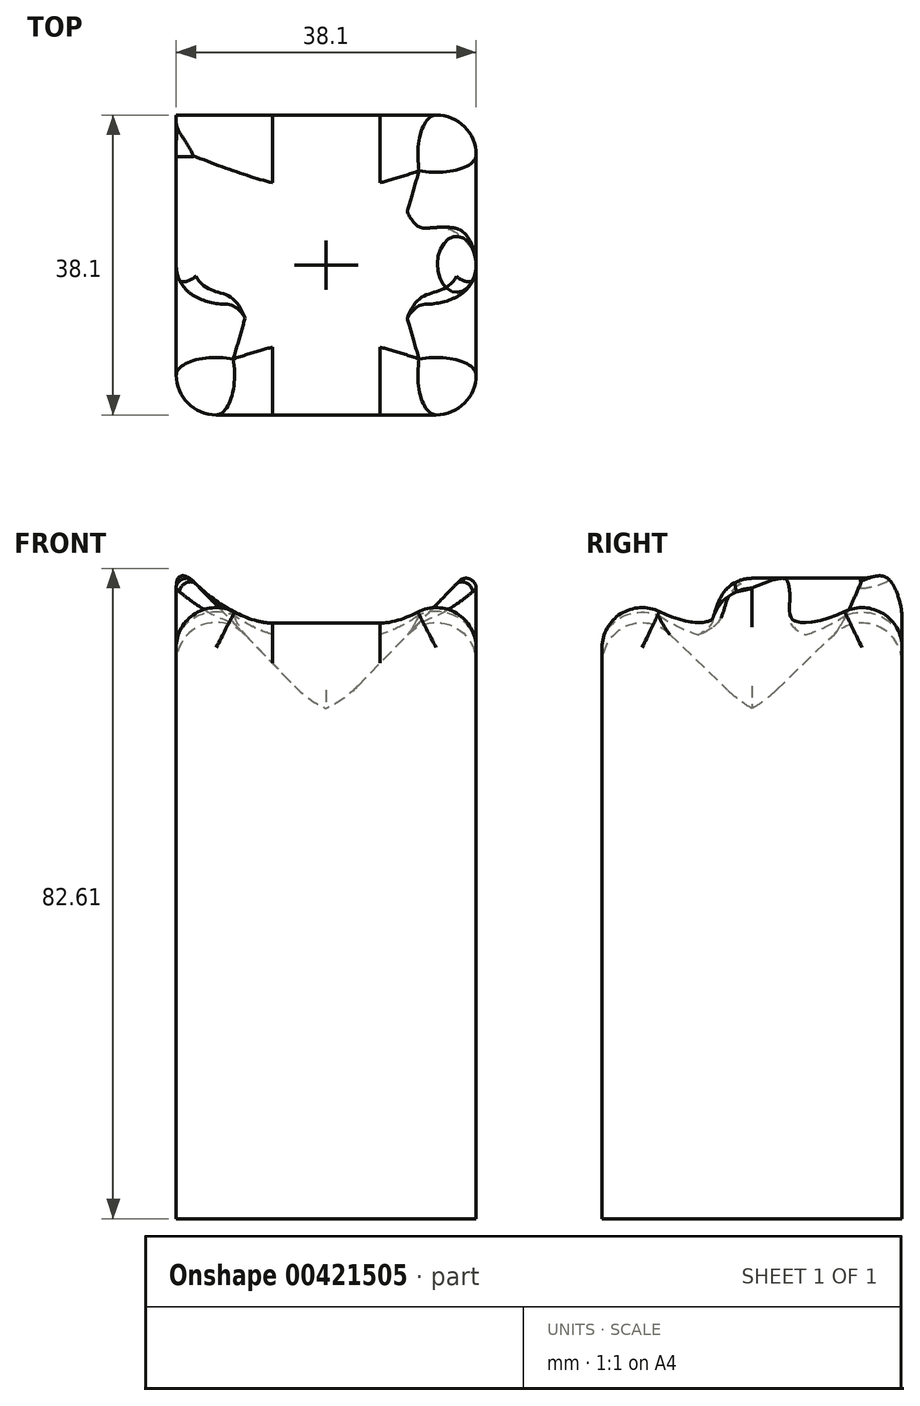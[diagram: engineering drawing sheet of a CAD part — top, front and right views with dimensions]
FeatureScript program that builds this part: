
annotation { "Feature Type Name" : "Feature", "Feature Type Description" : "" }
export const myFeature = defineFeature(function(context is Context, id is Id, definition is map)
    precondition{}
    {
        {
            var Q0;
            Q0=qCreatedBy(makeId("Top.planeOp"),FACE);
            var sketch = newSketch(context, id + "F0", { "sketchPlane" : qUnion([Q0])});
            skLineSegment(sketch, "E0.bottom", {"start": v(19.05, -19.05) * mm, "end": v(-19.05, -19.05) * mm});
            skLineSegment(sketch, "E0.top", {"start": v(19.05, 19.05) * mm, "end": v(-19.05, 19.05) * mm});
            skLineSegment(sketch, "E0.left", {"start": v(19.05, -19.05) * mm, "end": v(19.05, 19.05) * mm});
            skLineSegment(sketch, "E0.right", {"start": v(-19.05, -19.05) * mm, "end": v(-19.05, 19.05) * mm});
            skPoint(sketch, "E0.middle", {"position": v(0, 0) * mm});
            skSolve(sketch);
        }
        {
            var Q0;
            Q0=makeQuery(id+"F0.imprint","IMPRINT",FACE,{"disambiguationData":[TD([[makeQuery(id+"F0.imprint","IMPRINT",EDGE,{"derivedFrom":sQuery(id+"F0.wireOp",EDGE,"E0.bottom")}),-1.0]])]});
            extrude(context, id + "F1", {"entities" : qUnion([Q0]), "depth" : 63.5 * mm});
        }
        {
            var Q0;
            Q0=makeQuery(id+"F1.opExtrude","CAP_FACE",FACE,{"disambiguationData":[OSD([sQuery(id+"F0.wireOp",EDGE,"E0.bottom"),sQuery(id+"F0.wireOp",EDGE,"E0.top"),sQuery(id+"F0.wireOp",EDGE,"E0.left"),sQuery(id+"F0.wireOp",EDGE,"E0.right")])],"isStart":false});
            var sketch = newSketch(context, id + "F2", { "sketchPlane" : qUnion([Q0])});
            skLineSegment(sketch, "E1", {"start": v(0, 0) * mm, "end": v(0, 19.05) * mm});
            skLineSegment(sketch, "E2", {"start": v(0, 0) * mm, "end": v(0, -19.05) * mm});
            skLineSegment(sketch, "E3", {"start": v(0, 0) * mm, "end": v(-19.05, 0) * mm});
            skLineSegment(sketch, "E4", {"start": v(-19.05, 0) * mm, "end": v(0, 0) * mm});
            skLineSegment(sketch, "E5", {"start": v(0, 0) * mm, "end": v(19.05, 0) * mm});
            skSolve(sketch);
        }
        {
            var Q0;
            {var subQ0=sQuery(id+"F2.wireOp",EDGE,"E1");Q0=makeQuery(id+"F2.imprint","IMPRINT",FACE,{"disambiguationData":[TD([[makeQuery(id+"F2.imprint","IMPRINT",EDGE,{"derivedFrom":subQ0}),1.0]])]});}
            var Q1;
            {var subQ0=sQuery(id+"F2.wireOp",EDGE,"E2");Q1=makeQuery(id+"F2.imprint","IMPRINT",FACE,{"disambiguationData":[TD([[makeQuery(id+"F2.imprint","IMPRINT",EDGE,{"derivedFrom":subQ0}),-1.0]])]});}
            extrude(context, id + "F3", {"entities" : qUnion([Q0, Q1]), "operationType" : NewBodyOperationType.ADD, "depth" : 19.05 * mm});
        }
        {
            var Q0;
            Q0=makeQuery(id+"F3.opExtrude","CAP_EDGE",EDGE,{"disambiguationData":[OSD([sQuery(id+"F2.wireOp",EDGE,"E1"),sQuery(id+"F2.wireOp",EDGE,"E2")])],"isStart":false});
            chamfer(context, id + "F4", {"entities" : qUnion([Q0]), "chamferType" : ChamferType.OFFSET_ANGLE, "width" : 19.05 * mm, "oppositeDirection" : true, "angle" : 44 * degree, "tangentPropagation" : true});
        }
        {
            var Q0;
            Q0=makeQuery(id+"F1.opExtrude","CAP_FACE",FACE,{"disambiguationData":[OSD([sQuery(id+"F0.wireOp",EDGE,"E0.bottom"),sQuery(id+"F0.wireOp",EDGE,"E0.top"),sQuery(id+"F0.wireOp",EDGE,"E0.left"),sQuery(id+"F0.wireOp",EDGE,"E0.right")])],"isStart":false});
            extrude(context, id + "F5", {"entities" : qUnion([Q0]), "operationType" : NewBodyOperationType.ADD, "depth" : 19.05 * mm});
        }
        {
            var Q0;
            Q0=makeQuery(id+"F5.opExtrude","CAP_EDGE",EDGE,{"disambiguationData":[OSD([sQuery(id+"F0.wireOp",EDGE,"E0.bottom"),sQuery(id+"F0.wireOp",EDGE,"E0.top"),sQuery(id+"F0.wireOp",EDGE,"E0.left"),sQuery(id+"F0.wireOp",EDGE,"E0.right"),sQuery(id+"F2.wireOp",EDGE,"E1"),sQuery(id+"F2.wireOp",EDGE,"E2")])],"isStart":false});
            chamfer(context, id + "F6", {"entities" : qUnion([Q0]), "chamferType" : ChamferType.OFFSET_ANGLE, "width" : 19.05 * mm, "oppositeDirection" : false, "angle" : 44 * degree, "tangentPropagation" : true});
        }
        {
            var Q0;
            {var subQ0=sQuery(id+"F2.wireOp",EDGE,"E1");Q0=makeQuery(id+"F2.imprint","IMPRINT",FACE,{"disambiguationData":[TD([[makeQuery(id+"F2.imprint","IMPRINT",EDGE,{"derivedFrom":subQ0}),1.0]])]});}
            var Q1;
            {var subQ0=sQuery(id+"F2.wireOp",EDGE,"E1");Q1=makeQuery(id+"F2.imprint","IMPRINT",FACE,{"disambiguationData":[TD([[makeQuery(id+"F2.imprint","IMPRINT",EDGE,{"derivedFrom":subQ0}),-1.0]])]});}
            extrude(context, id + "F7", {"entities" : qUnion([Q0, Q1]), "operationType" : NewBodyOperationType.ADD, "depth" : 19.05 * mm});
        }
        {
            var Q0;
            Q0=makeQuery(id+"F7.opExtrude","CAP_EDGE",EDGE,{"disambiguationData":[OSD([sQuery(id+"F2.wireOp",EDGE,"E4"),sQuery(id+"F2.wireOp",EDGE,"E5")])],"isStart":false});
            chamfer(context, id + "F8", {"entities" : qUnion([Q0]), "chamferType" : ChamferType.OFFSET_ANGLE, "width" : 19.05 * mm, "oppositeDirection" : true, "angle" : 44 * degree, "tangentPropagation" : true});
        }
        {
            var Q0;
            {var subQ0=sQuery(id+"F2.wireOp",EDGE,"E2");Q0=makeQuery(id+"F2.imprint","IMPRINT",FACE,{"disambiguationData":[TD([[makeQuery(id+"F2.imprint","IMPRINT",EDGE,{"derivedFrom":subQ0}),-1.0]])]});}
            var Q1;
            {var subQ0=sQuery(id+"F2.wireOp",EDGE,"E2");Q1=makeQuery(id+"F2.imprint","IMPRINT",FACE,{"disambiguationData":[TD([[makeQuery(id+"F2.imprint","IMPRINT",EDGE,{"derivedFrom":subQ0}),1.0]])]});}
            extrude(context, id + "F9", {"entities" : qUnion([Q0, Q1]), "operationType" : NewBodyOperationType.ADD, "depth" : 19.05 * mm});
        }
        {
            var Q0;
            Q0=makeQuery(id+"F9.opExtrude","CAP_EDGE",EDGE,{"disambiguationData":[OSD([sQuery(id+"F2.wireOp",EDGE,"E4"),sQuery(id+"F2.wireOp",EDGE,"E5")])],"isStart":false});
            chamfer(context, id + "F10", {"entities" : qUnion([Q0]), "chamferType" : ChamferType.OFFSET_ANGLE, "width" : 19.05 * mm, "oppositeDirection" : false, "angle" : 44 * degree, "tangentPropagation" : true});
        }
        {
            var Q0;
            Q0=makeQuery(id+"F10.opChamfer","BLEND_EDGE",EDGE,{"blendedFrom":[makeQuery(id+"F9.opExtrude","CAP_EDGE",EDGE,{"disambiguationData":[OSD([sQuery(id+"F2.wireOp",EDGE,"E4"),sQuery(id+"F2.wireOp",EDGE,"E5")])],"isStart":false}),makeQuery(id+"F6.opChamfer","BLEND_FACE",FACE,{"disambiguationData":[OSD([sQuery(id+"F0.wireOp",EDGE,"E0.bottom"),sQuery(id+"F0.wireOp",EDGE,"E0.top"),sQuery(id+"F0.wireOp",EDGE,"E0.left"),sQuery(id+"F0.wireOp",EDGE,"E0.right"),sQuery(id+"F2.wireOp",EDGE,"E1"),sQuery(id+"F2.wireOp",EDGE,"E2")])]})],"blendedInto":[makeQuery(id+"F6.opChamfer","BLEND_FACE",FACE,{"disambiguationData":[OSD([sQuery(id+"F0.wireOp",EDGE,"E0.bottom"),sQuery(id+"F0.wireOp",EDGE,"E0.top"),sQuery(id+"F0.wireOp",EDGE,"E0.left"),sQuery(id+"F0.wireOp",EDGE,"E0.right"),sQuery(id+"F2.wireOp",EDGE,"E1"),sQuery(id+"F2.wireOp",EDGE,"E2")])]})]});
            var Q1;
            Q1=makeQuery(id+"F8.opChamfer","BLEND_EDGE",EDGE,{"blendedFrom":[makeQuery(id+"F7.opExtrude","CAP_EDGE",EDGE,{"disambiguationData":[OSD([sQuery(id+"F2.wireOp",EDGE,"E4"),sQuery(id+"F2.wireOp",EDGE,"E5")])],"isStart":false}),makeQuery(id+"F6.opChamfer","BLEND_FACE",FACE,{"disambiguationData":[OSD([sQuery(id+"F0.wireOp",EDGE,"E0.bottom"),sQuery(id+"F0.wireOp",EDGE,"E0.top"),sQuery(id+"F0.wireOp",EDGE,"E0.left"),sQuery(id+"F0.wireOp",EDGE,"E0.right"),sQuery(id+"F2.wireOp",EDGE,"E1"),sQuery(id+"F2.wireOp",EDGE,"E2")])]})],"blendedInto":[makeQuery(id+"F6.opChamfer","BLEND_FACE",FACE,{"disambiguationData":[OSD([sQuery(id+"F0.wireOp",EDGE,"E0.bottom"),sQuery(id+"F0.wireOp",EDGE,"E0.top"),sQuery(id+"F0.wireOp",EDGE,"E0.left"),sQuery(id+"F0.wireOp",EDGE,"E0.right"),sQuery(id+"F2.wireOp",EDGE,"E1"),sQuery(id+"F2.wireOp",EDGE,"E2")])]})]});
            var Q2;
            Q2=makeQuery(id+"F8.opChamfer","BLEND_EDGE",EDGE,{"blendedFrom":[makeQuery(id+"F7.opExtrude","CAP_EDGE",EDGE,{"disambiguationData":[OSD([sQuery(id+"F2.wireOp",EDGE,"E4"),sQuery(id+"F2.wireOp",EDGE,"E5")])],"isStart":false}),makeQuery(id+"F4.opChamfer","BLEND_FACE",FACE,{"disambiguationData":[OSD([sQuery(id+"F2.wireOp",EDGE,"E1"),sQuery(id+"F2.wireOp",EDGE,"E2")])]})],"blendedInto":[makeQuery(id+"F4.opChamfer","BLEND_FACE",FACE,{"disambiguationData":[OSD([sQuery(id+"F2.wireOp",EDGE,"E1"),sQuery(id+"F2.wireOp",EDGE,"E2")])]})]});
            var Q3;
            Q3=makeQuery(id+"F10.opChamfer","BLEND_EDGE",EDGE,{"blendedFrom":[makeQuery(id+"F9.opExtrude","CAP_EDGE",EDGE,{"disambiguationData":[OSD([sQuery(id+"F2.wireOp",EDGE,"E4"),sQuery(id+"F2.wireOp",EDGE,"E5")])],"isStart":false}),makeQuery(id+"F4.opChamfer","BLEND_FACE",FACE,{"disambiguationData":[OSD([sQuery(id+"F2.wireOp",EDGE,"E1"),sQuery(id+"F2.wireOp",EDGE,"E2")])]})],"blendedInto":[makeQuery(id+"F4.opChamfer","BLEND_FACE",FACE,{"disambiguationData":[OSD([sQuery(id+"F2.wireOp",EDGE,"E1"),sQuery(id+"F2.wireOp",EDGE,"E2")])]})]});
            fillet(context, id + "F11", {"entities" : qUnion([Q0, Q1, Q2, Q3]), "radius" : 5.08 * mm, "tangentPropagation" : true, "allowEdgeOverflow" : false});
        }
        {
            var Q0;
            Q0=makeQuery(id+"F3.opExtrude","CAP_EDGE",EDGE,{"disambiguationData":[OSD([sQuery(id+"F0.wireOp",EDGE,"E0.right")])],"isStart":false});
            var Q1;
            {var subQ0=sQuery(id+"F0.wireOp",EDGE,"E0.top");Q1=makeQuery(id+"F7.boolean.opBoolean","MERGE",EDGE,{"derivedFrom":[makeQuery(id+"F3.opExtrude","CAP_EDGE",EDGE,{"disambiguationData":[OSD([subQ0])],"isStart":false}),makeQuery(id+"F5.opExtrude","CAP_EDGE",EDGE,{"disambiguationData":[OSD([subQ0])],"isStart":false}),makeQuery(id+"F7.opExtrude","CAP_EDGE",EDGE,{"disambiguationData":[OSD([subQ0])],"isStart":false})]});}
            var Q2;
            Q2=makeQuery(id+"F5.opExtrude","CAP_EDGE",EDGE,{"disambiguationData":[OSD([sQuery(id+"F0.wireOp",EDGE,"E0.left")])],"isStart":false});
            var Q3;
            {var subQ0=sQuery(id+"F0.wireOp",EDGE,"E0.bottom");Q3=makeQuery(id+"F9.boolean.opBoolean","MERGE",EDGE,{"derivedFrom":[makeQuery(id+"F3.opExtrude","CAP_EDGE",EDGE,{"disambiguationData":[OSD([subQ0])],"isStart":false}),makeQuery(id+"F5.opExtrude","CAP_EDGE",EDGE,{"disambiguationData":[OSD([subQ0])],"isStart":false}),makeQuery(id+"F9.opExtrude","CAP_EDGE",EDGE,{"disambiguationData":[OSD([subQ0])],"isStart":false})]});}
            fillet(context, id + "F12", {"entities" : qUnion([Q0, Q1, Q2, Q3]), "radius" : 5.08 * mm, "tangentPropagation" : true, "allowEdgeOverflow" : false});
        }
        {
            var Q0;
            {var subQ0=sQuery(id+"F0.wireOp",EDGE,"E0.top");Q0=makeQuery(id+"F12.opFillet","BLEND_EDGE",EDGE,{"blendedFrom":[makeQuery(id+"F7.boolean.opBoolean","MERGE",EDGE,{"derivedFrom":[makeQuery(id+"F3.opExtrude","CAP_EDGE",EDGE,{"disambiguationData":[OSD([subQ0])],"isStart":false}),makeQuery(id+"F5.opExtrude","CAP_EDGE",EDGE,{"disambiguationData":[OSD([subQ0])],"isStart":false}),makeQuery(id+"F7.opExtrude","CAP_EDGE",EDGE,{"disambiguationData":[OSD([subQ0])],"isStart":false})]}),makeQuery(id+"F3.opExtrude","CAP_EDGE",EDGE,{"disambiguationData":[OSD([sQuery(id+"F0.wireOp",EDGE,"E0.right")])],"isStart":false})],"blendedInto":[]});}
            var Q1;
            {var subQ0=sQuery(id+"F0.wireOp",EDGE,"E0.left");var subQ1=sQuery(id+"F0.wireOp",EDGE,"E0.top");Q1=makeQuery(id+"F5.boolean.opBoolean","MERGE",EDGE,{"derivedFrom":[makeQuery(id+"F1.opExtrude","SWEPT_EDGE",EDGE,{"disambiguationData":[OSD([subQ1,subQ0])]}),makeQuery(id+"F5.opExtrude","SWEPT_EDGE",EDGE,{"disambiguationData":[OSD([subQ1,subQ0])]})]});}
            var Q2;
            {var subQ0=sQuery(id+"F0.wireOp",EDGE,"E0.left");var subQ1=sQuery(id+"F0.wireOp",EDGE,"E0.bottom");Q2=makeQuery(id+"F5.boolean.opBoolean","MERGE",EDGE,{"derivedFrom":[makeQuery(id+"F1.opExtrude","SWEPT_EDGE",EDGE,{"disambiguationData":[OSD([subQ1,subQ0])]}),makeQuery(id+"F5.opExtrude","SWEPT_EDGE",EDGE,{"disambiguationData":[OSD([subQ1,subQ0])]})]});}
            var Q3;
            {var subQ0=sQuery(id+"F0.wireOp",EDGE,"E0.right");var subQ1=sQuery(id+"F0.wireOp",EDGE,"E0.bottom");Q3=makeQuery(id+"F3.boolean.opBoolean","MERGE",EDGE,{"derivedFrom":[makeQuery(id+"F1.opExtrude","SWEPT_EDGE",EDGE,{"disambiguationData":[OSD([subQ1,subQ0])]}),makeQuery(id+"F3.opExtrude","SWEPT_EDGE",EDGE,{"disambiguationData":[OSD([subQ1,subQ0])]})]});}
            fillet(context, id + "F13", {"entities" : qUnion([Q0, Q1, Q2, Q3]), "radius" : 5.08 * mm, "tangentPropagation" : true, "allowEdgeOverflow" : false});
        }
        {
            var Q0;
            {var subQ0=sQuery(id+"F0.wireOp",EDGE,"E0.left");Q0=makeQuery(id+"F12.opFillet","BLEND_EDGE",EDGE,{"blendedFrom":[makeQuery(id+"F5.opExtrude","CAP_EDGE",EDGE,{"disambiguationData":[OSD([subQ0])],"isStart":false}),makeQuery(id+"F6.opChamfer","BLEND_FACE",FACE,{"disambiguationData":[OSD([sQuery(id+"F0.wireOp",EDGE,"E0.bottom"),sQuery(id+"F0.wireOp",EDGE,"E0.top"),subQ0,sQuery(id+"F0.wireOp",EDGE,"E0.right"),sQuery(id+"F2.wireOp",EDGE,"E1"),sQuery(id+"F2.wireOp",EDGE,"E2")])]})],"blendedInto":[makeQuery(id+"F6.opChamfer","BLEND_FACE",FACE,{"disambiguationData":[OSD([sQuery(id+"F0.wireOp",EDGE,"E0.bottom"),sQuery(id+"F0.wireOp",EDGE,"E0.top"),subQ0,sQuery(id+"F0.wireOp",EDGE,"E0.right"),sQuery(id+"F2.wireOp",EDGE,"E1"),sQuery(id+"F2.wireOp",EDGE,"E2")])]})]});}
            var Q1;
            {var subQ0=sQuery(id+"F0.wireOp",EDGE,"E0.top");Q1=makeQuery(id+"F12.opFillet","BLEND_EDGE",EDGE,{"blendedFrom":[makeQuery(id+"F7.boolean.opBoolean","MERGE",EDGE,{"derivedFrom":[makeQuery(id+"F3.opExtrude","CAP_EDGE",EDGE,{"disambiguationData":[OSD([subQ0])],"isStart":false}),makeQuery(id+"F5.opExtrude","CAP_EDGE",EDGE,{"disambiguationData":[OSD([subQ0])],"isStart":false}),makeQuery(id+"F7.opExtrude","CAP_EDGE",EDGE,{"disambiguationData":[OSD([subQ0])],"isStart":false})]}),makeQuery(id+"F8.opChamfer","BLEND_FACE",FACE,{"disambiguationData":[OSD([sQuery(id+"F2.wireOp",EDGE,"E4"),sQuery(id+"F2.wireOp",EDGE,"E5")])]})],"blendedInto":[makeQuery(id+"F8.opChamfer","BLEND_FACE",FACE,{"disambiguationData":[OSD([sQuery(id+"F2.wireOp",EDGE,"E4"),sQuery(id+"F2.wireOp",EDGE,"E5")])]})]});}
            var Q2;
            Q2=makeQuery(id+"F12.opFillet","BLEND_EDGE",EDGE,{"blendedFrom":[makeQuery(id+"F3.opExtrude","CAP_EDGE",EDGE,{"disambiguationData":[OSD([sQuery(id+"F0.wireOp",EDGE,"E0.right")])],"isStart":false}),makeQuery(id+"F4.opChamfer","BLEND_FACE",FACE,{"disambiguationData":[OSD([sQuery(id+"F2.wireOp",EDGE,"E1"),sQuery(id+"F2.wireOp",EDGE,"E2")])]})],"blendedInto":[makeQuery(id+"F4.opChamfer","BLEND_FACE",FACE,{"disambiguationData":[OSD([sQuery(id+"F2.wireOp",EDGE,"E1"),sQuery(id+"F2.wireOp",EDGE,"E2")])]})]});
            var Q3;
            {var subQ0=sQuery(id+"F0.wireOp",EDGE,"E0.bottom");Q3=makeQuery(id+"F12.opFillet","BLEND_EDGE",EDGE,{"blendedFrom":[makeQuery(id+"F9.boolean.opBoolean","MERGE",EDGE,{"derivedFrom":[makeQuery(id+"F3.opExtrude","CAP_EDGE",EDGE,{"disambiguationData":[OSD([subQ0])],"isStart":false}),makeQuery(id+"F5.opExtrude","CAP_EDGE",EDGE,{"disambiguationData":[OSD([subQ0])],"isStart":false}),makeQuery(id+"F9.opExtrude","CAP_EDGE",EDGE,{"disambiguationData":[OSD([subQ0])],"isStart":false})]}),makeQuery(id+"F10.opChamfer","BLEND_FACE",FACE,{"disambiguationData":[OSD([sQuery(id+"F2.wireOp",EDGE,"E4"),sQuery(id+"F2.wireOp",EDGE,"E5")])]})],"blendedInto":[makeQuery(id+"F10.opChamfer","BLEND_FACE",FACE,{"disambiguationData":[OSD([sQuery(id+"F2.wireOp",EDGE,"E4"),sQuery(id+"F2.wireOp",EDGE,"E5")])]})]});}
            var Q4;
            {var subQ0=sQuery(id+"F2.wireOp",EDGE,"E2");var subQ1=sQuery(id+"F2.wireOp",EDGE,"E1");var subQ2=sQuery(id+"F2.wireOp",EDGE,"E5");var subQ3=sQuery(id+"F2.wireOp",EDGE,"E4");var subQ4=sQuery(id+"F0.wireOp",EDGE,"E0.bottom");Q4=makeQuery(id+"F13.opFillet","BLEND_EDGE",EDGE,{"blendedFrom":[makeQuery(id+"F12.opFillet","BLEND_EDGE",EDGE,{"blendedFrom":[makeQuery(id+"F9.boolean.opBoolean","MERGE",EDGE,{"derivedFrom":[makeQuery(id+"F3.opExtrude","CAP_EDGE",EDGE,{"disambiguationData":[OSD([subQ4])],"isStart":false}),makeQuery(id+"F5.opExtrude","CAP_EDGE",EDGE,{"disambiguationData":[OSD([subQ4])],"isStart":false}),makeQuery(id+"F9.opExtrude","CAP_EDGE",EDGE,{"disambiguationData":[OSD([subQ4])],"isStart":false})]}),makeQuery(id+"F3.opExtrude","CAP_EDGE",EDGE,{"disambiguationData":[OSD([sQuery(id+"F0.wireOp",EDGE,"E0.right")])],"isStart":false})],"blendedInto":[]}),makeQuery(id+"F11.opFillet","BLEND_FACE",FACE,{"disambiguationData":[OSD([subQ1,subQ0,subQ3,subQ2]),TDD([makeQuery(id+"F10.opChamfer","BLEND_EDGE",EDGE,{"blendedFrom":[makeQuery(id+"F9.opExtrude","CAP_EDGE",EDGE,{"disambiguationData":[OSD([subQ3,subQ2])],"isStart":false}),makeQuery(id+"F4.opChamfer","BLEND_FACE",FACE,{"disambiguationData":[OSD([subQ1,subQ0])]})],"blendedInto":[makeQuery(id+"F4.opChamfer","BLEND_FACE",FACE,{"disambiguationData":[OSD([subQ1,subQ0])]})]})])]})],"blendedInto":[makeQuery(id+"F11.opFillet","BLEND_FACE",FACE,{"disambiguationData":[OSD([subQ1,subQ0,subQ3,subQ2]),TDD([makeQuery(id+"F10.opChamfer","BLEND_EDGE",EDGE,{"blendedFrom":[makeQuery(id+"F9.opExtrude","CAP_EDGE",EDGE,{"disambiguationData":[OSD([subQ3,subQ2])],"isStart":false}),makeQuery(id+"F4.opChamfer","BLEND_FACE",FACE,{"disambiguationData":[OSD([subQ1,subQ0])]})],"blendedInto":[makeQuery(id+"F4.opChamfer","BLEND_FACE",FACE,{"disambiguationData":[OSD([subQ1,subQ0])]})]})])]})]});}
            var Q5;
            {var subQ0=sQuery(id+"F2.wireOp",EDGE,"E2");var subQ1=sQuery(id+"F2.wireOp",EDGE,"E1");var subQ2=sQuery(id+"F2.wireOp",EDGE,"E5");var subQ3=sQuery(id+"F2.wireOp",EDGE,"E4");var subQ4=sQuery(id+"F0.wireOp",EDGE,"E0.top");Q5=makeQuery(id+"F13.opFillet","BLEND_EDGE",EDGE,{"blendedFrom":[makeQuery(id+"F12.opFillet","BLEND_EDGE",EDGE,{"blendedFrom":[makeQuery(id+"F7.boolean.opBoolean","MERGE",EDGE,{"derivedFrom":[makeQuery(id+"F3.opExtrude","CAP_EDGE",EDGE,{"disambiguationData":[OSD([subQ4])],"isStart":false}),makeQuery(id+"F5.opExtrude","CAP_EDGE",EDGE,{"disambiguationData":[OSD([subQ4])],"isStart":false}),makeQuery(id+"F7.opExtrude","CAP_EDGE",EDGE,{"disambiguationData":[OSD([subQ4])],"isStart":false})]}),makeQuery(id+"F3.opExtrude","CAP_EDGE",EDGE,{"disambiguationData":[OSD([sQuery(id+"F0.wireOp",EDGE,"E0.right")])],"isStart":false})],"blendedInto":[]}),makeQuery(id+"F11.opFillet","BLEND_FACE",FACE,{"disambiguationData":[OSD([subQ1,subQ0,subQ3,subQ2]),TDD([makeQuery(id+"F8.opChamfer","BLEND_EDGE",EDGE,{"blendedFrom":[makeQuery(id+"F7.opExtrude","CAP_EDGE",EDGE,{"disambiguationData":[OSD([subQ3,subQ2])],"isStart":false}),makeQuery(id+"F4.opChamfer","BLEND_FACE",FACE,{"disambiguationData":[OSD([subQ1,subQ0])]})],"blendedInto":[makeQuery(id+"F4.opChamfer","BLEND_FACE",FACE,{"disambiguationData":[OSD([subQ1,subQ0])]})]})])]})],"blendedInto":[makeQuery(id+"F11.opFillet","BLEND_FACE",FACE,{"disambiguationData":[OSD([subQ1,subQ0,subQ3,subQ2]),TDD([makeQuery(id+"F8.opChamfer","BLEND_EDGE",EDGE,{"blendedFrom":[makeQuery(id+"F7.opExtrude","CAP_EDGE",EDGE,{"disambiguationData":[OSD([subQ3,subQ2])],"isStart":false}),makeQuery(id+"F4.opChamfer","BLEND_FACE",FACE,{"disambiguationData":[OSD([subQ1,subQ0])]})],"blendedInto":[makeQuery(id+"F4.opChamfer","BLEND_FACE",FACE,{"disambiguationData":[OSD([subQ1,subQ0])]})]})])]})]});}
            var Q6;
            {var subQ0=sQuery(id+"F2.wireOp",EDGE,"E2");var subQ1=sQuery(id+"F2.wireOp",EDGE,"E1");var subQ2=sQuery(id+"F0.wireOp",EDGE,"E0.right");var subQ3=sQuery(id+"F0.wireOp",EDGE,"E0.left");var subQ4=sQuery(id+"F0.wireOp",EDGE,"E0.top");var subQ5=sQuery(id+"F0.wireOp",EDGE,"E0.bottom");var subQ6=sQuery(id+"F2.wireOp",EDGE,"E5");var subQ7=sQuery(id+"F2.wireOp",EDGE,"E4");Q6=makeQuery(id+"F13.opFillet","BLEND_EDGE",EDGE,{"blendedFrom":[makeQuery(id+"F12.opFillet","BLEND_EDGE",EDGE,{"blendedFrom":[makeQuery(id+"F7.boolean.opBoolean","MERGE",EDGE,{"derivedFrom":[makeQuery(id+"F3.opExtrude","CAP_EDGE",EDGE,{"disambiguationData":[OSD([subQ4])],"isStart":false}),makeQuery(id+"F5.opExtrude","CAP_EDGE",EDGE,{"disambiguationData":[OSD([subQ4])],"isStart":false}),makeQuery(id+"F7.opExtrude","CAP_EDGE",EDGE,{"disambiguationData":[OSD([subQ4])],"isStart":false})]}),makeQuery(id+"F5.opExtrude","CAP_EDGE",EDGE,{"disambiguationData":[OSD([subQ3])],"isStart":false})],"blendedInto":[]}),makeQuery(id+"F11.opFillet","BLEND_FACE",FACE,{"disambiguationData":[OSD([subQ5,subQ4,subQ3,subQ2,subQ1,subQ0,subQ7,subQ6]),TDD([makeQuery(id+"F8.opChamfer","BLEND_EDGE",EDGE,{"blendedFrom":[makeQuery(id+"F7.opExtrude","CAP_EDGE",EDGE,{"disambiguationData":[OSD([subQ7,subQ6])],"isStart":false}),makeQuery(id+"F6.opChamfer","BLEND_FACE",FACE,{"disambiguationData":[OSD([subQ5,subQ4,subQ3,subQ2,subQ1,subQ0])]})],"blendedInto":[makeQuery(id+"F6.opChamfer","BLEND_FACE",FACE,{"disambiguationData":[OSD([subQ5,subQ4,subQ3,subQ2,subQ1,subQ0])]})]})])]})],"blendedInto":[makeQuery(id+"F11.opFillet","BLEND_FACE",FACE,{"disambiguationData":[OSD([subQ5,subQ4,subQ3,subQ2,subQ1,subQ0,subQ7,subQ6]),TDD([makeQuery(id+"F8.opChamfer","BLEND_EDGE",EDGE,{"blendedFrom":[makeQuery(id+"F7.opExtrude","CAP_EDGE",EDGE,{"disambiguationData":[OSD([subQ7,subQ6])],"isStart":false}),makeQuery(id+"F6.opChamfer","BLEND_FACE",FACE,{"disambiguationData":[OSD([subQ5,subQ4,subQ3,subQ2,subQ1,subQ0])]})],"blendedInto":[makeQuery(id+"F6.opChamfer","BLEND_FACE",FACE,{"disambiguationData":[OSD([subQ5,subQ4,subQ3,subQ2,subQ1,subQ0])]})]})])]})]});}
            var Q7;
            {var subQ0=sQuery(id+"F2.wireOp",EDGE,"E2");var subQ1=sQuery(id+"F2.wireOp",EDGE,"E1");var subQ2=sQuery(id+"F0.wireOp",EDGE,"E0.right");var subQ3=sQuery(id+"F0.wireOp",EDGE,"E0.left");var subQ4=sQuery(id+"F0.wireOp",EDGE,"E0.top");var subQ5=sQuery(id+"F0.wireOp",EDGE,"E0.bottom");var subQ6=sQuery(id+"F2.wireOp",EDGE,"E5");var subQ7=sQuery(id+"F2.wireOp",EDGE,"E4");Q7=makeQuery(id+"F13.opFillet","BLEND_EDGE",EDGE,{"blendedFrom":[makeQuery(id+"F12.opFillet","BLEND_EDGE",EDGE,{"blendedFrom":[makeQuery(id+"F9.boolean.opBoolean","MERGE",EDGE,{"derivedFrom":[makeQuery(id+"F3.opExtrude","CAP_EDGE",EDGE,{"disambiguationData":[OSD([subQ5])],"isStart":false}),makeQuery(id+"F5.opExtrude","CAP_EDGE",EDGE,{"disambiguationData":[OSD([subQ5])],"isStart":false}),makeQuery(id+"F9.opExtrude","CAP_EDGE",EDGE,{"disambiguationData":[OSD([subQ5])],"isStart":false})]}),makeQuery(id+"F5.opExtrude","CAP_EDGE",EDGE,{"disambiguationData":[OSD([subQ3])],"isStart":false})],"blendedInto":[]}),makeQuery(id+"F11.opFillet","BLEND_FACE",FACE,{"disambiguationData":[OSD([subQ5,subQ4,subQ3,subQ2,subQ1,subQ0,subQ7,subQ6]),TDD([makeQuery(id+"F10.opChamfer","BLEND_EDGE",EDGE,{"blendedFrom":[makeQuery(id+"F9.opExtrude","CAP_EDGE",EDGE,{"disambiguationData":[OSD([subQ7,subQ6])],"isStart":false}),makeQuery(id+"F6.opChamfer","BLEND_FACE",FACE,{"disambiguationData":[OSD([subQ5,subQ4,subQ3,subQ2,subQ1,subQ0])]})],"blendedInto":[makeQuery(id+"F6.opChamfer","BLEND_FACE",FACE,{"disambiguationData":[OSD([subQ5,subQ4,subQ3,subQ2,subQ1,subQ0])]})]})])]})],"blendedInto":[makeQuery(id+"F11.opFillet","BLEND_FACE",FACE,{"disambiguationData":[OSD([subQ5,subQ4,subQ3,subQ2,subQ1,subQ0,subQ7,subQ6]),TDD([makeQuery(id+"F10.opChamfer","BLEND_EDGE",EDGE,{"blendedFrom":[makeQuery(id+"F9.opExtrude","CAP_EDGE",EDGE,{"disambiguationData":[OSD([subQ7,subQ6])],"isStart":false}),makeQuery(id+"F6.opChamfer","BLEND_FACE",FACE,{"disambiguationData":[OSD([subQ5,subQ4,subQ3,subQ2,subQ1,subQ0])]})],"blendedInto":[makeQuery(id+"F6.opChamfer","BLEND_FACE",FACE,{"disambiguationData":[OSD([subQ5,subQ4,subQ3,subQ2,subQ1,subQ0])]})]})])]})]});}
            fillet(context, id + "F14", {"entities" : qUnion([Q0, Q1, Q2, Q3, Q4, Q5, Q6, Q7]), "radius" : 1.27 * mm, "tangentPropagation" : true, "allowEdgeOverflow" : false});
        }
    });
